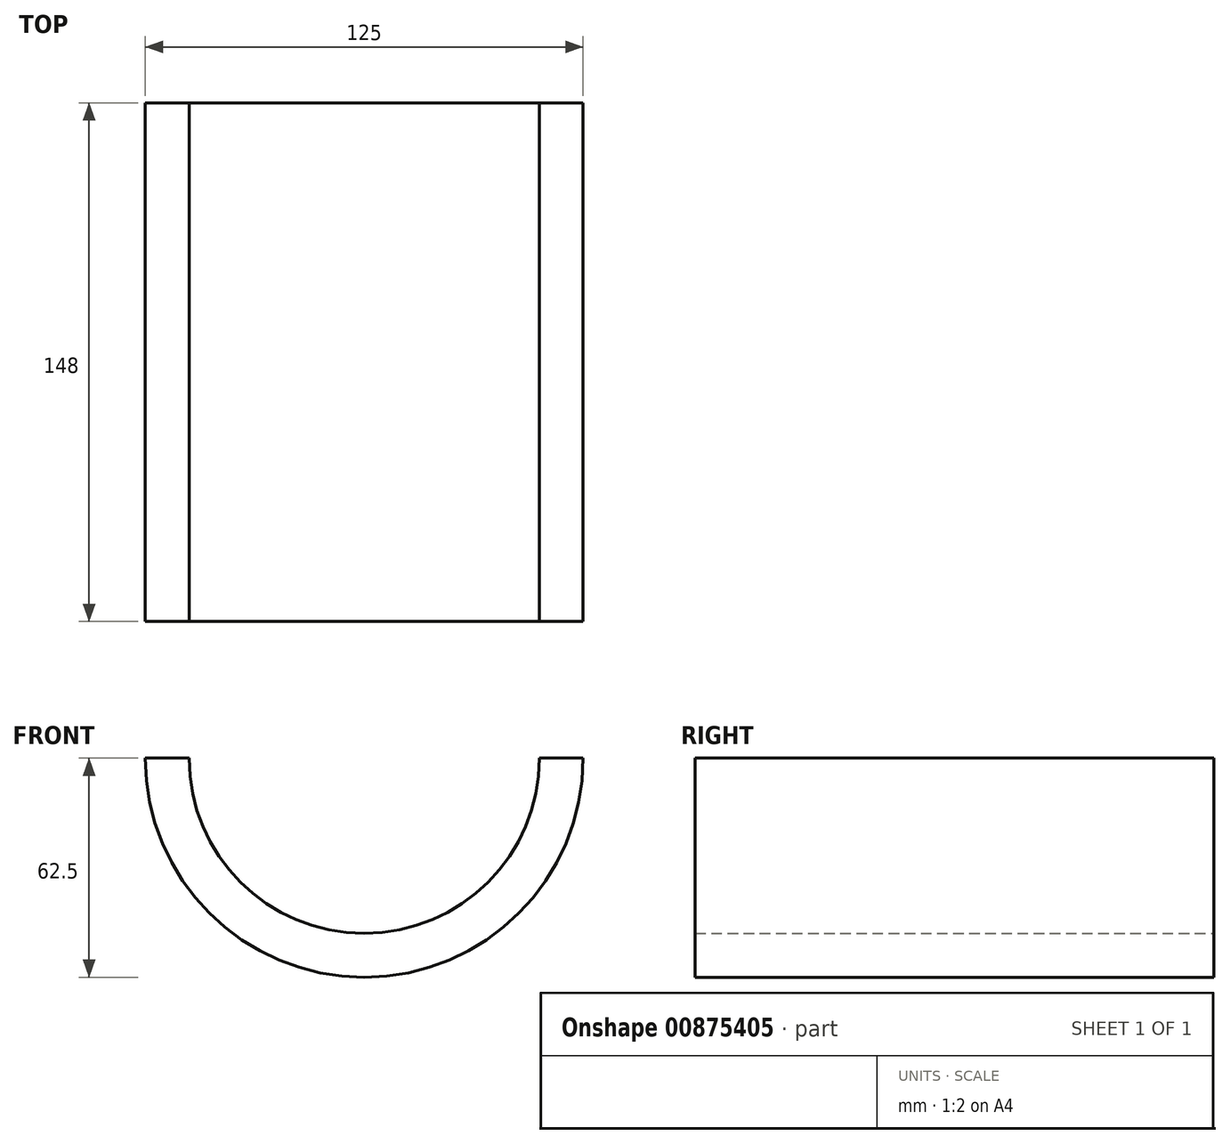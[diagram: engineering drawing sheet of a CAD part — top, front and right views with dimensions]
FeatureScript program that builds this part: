
annotation { "Feature Type Name" : "Feature", "Feature Type Description" : "" }
export const myFeature = defineFeature(function(context is Context, id is Id, definition is map)
    precondition{}
    {
        {
            var Q0;
            Q0=qCreatedBy(makeId("Front.planeOp"),FACE);
            var sketch = newSketch(context, id + "F0", { "sketchPlane" : qUnion([Q0])});
            skArc(sketch, "E0", {"start": v(-50, 0) * mm, "mid": v(0, -50) * mm, "end": v(50, 0) * mm});
            skArc(sketch, "E1", {"start": v(-62.5, 0) * mm, "mid": v(0, -62.5) * mm, "end": v(62.5, 0) * mm});
            skLineSegment(sketch, "E2", {"start": v(-50, 0) * mm, "end": v(-62.5, 0) * mm});
            skLineSegment(sketch, "E3", {"start": v(-62.5, 0) * mm, "end": v(-50, 0) * mm});
            skLineSegment(sketch, "E4", {"start": v(50, 0) * mm, "end": v(62.5, 0) * mm});
            skSolve(sketch);
        }
        {
            var Q0;
            Q0=makeQuery(id+"F0.imprint","IMPRINT",FACE,{"disambiguationData":[TD([[makeQuery(id+"F0.imprint","IMPRINT",EDGE,{"derivedFrom":sQuery(id+"F0.wireOp",EDGE,"E0")}),-1.0]])]});
            extrude(context, id + "F1", {"entities" : qUnion([Q0]), "depth" : 148 * mm, "offsetDistance" : 25 * mm});
        }
    });
